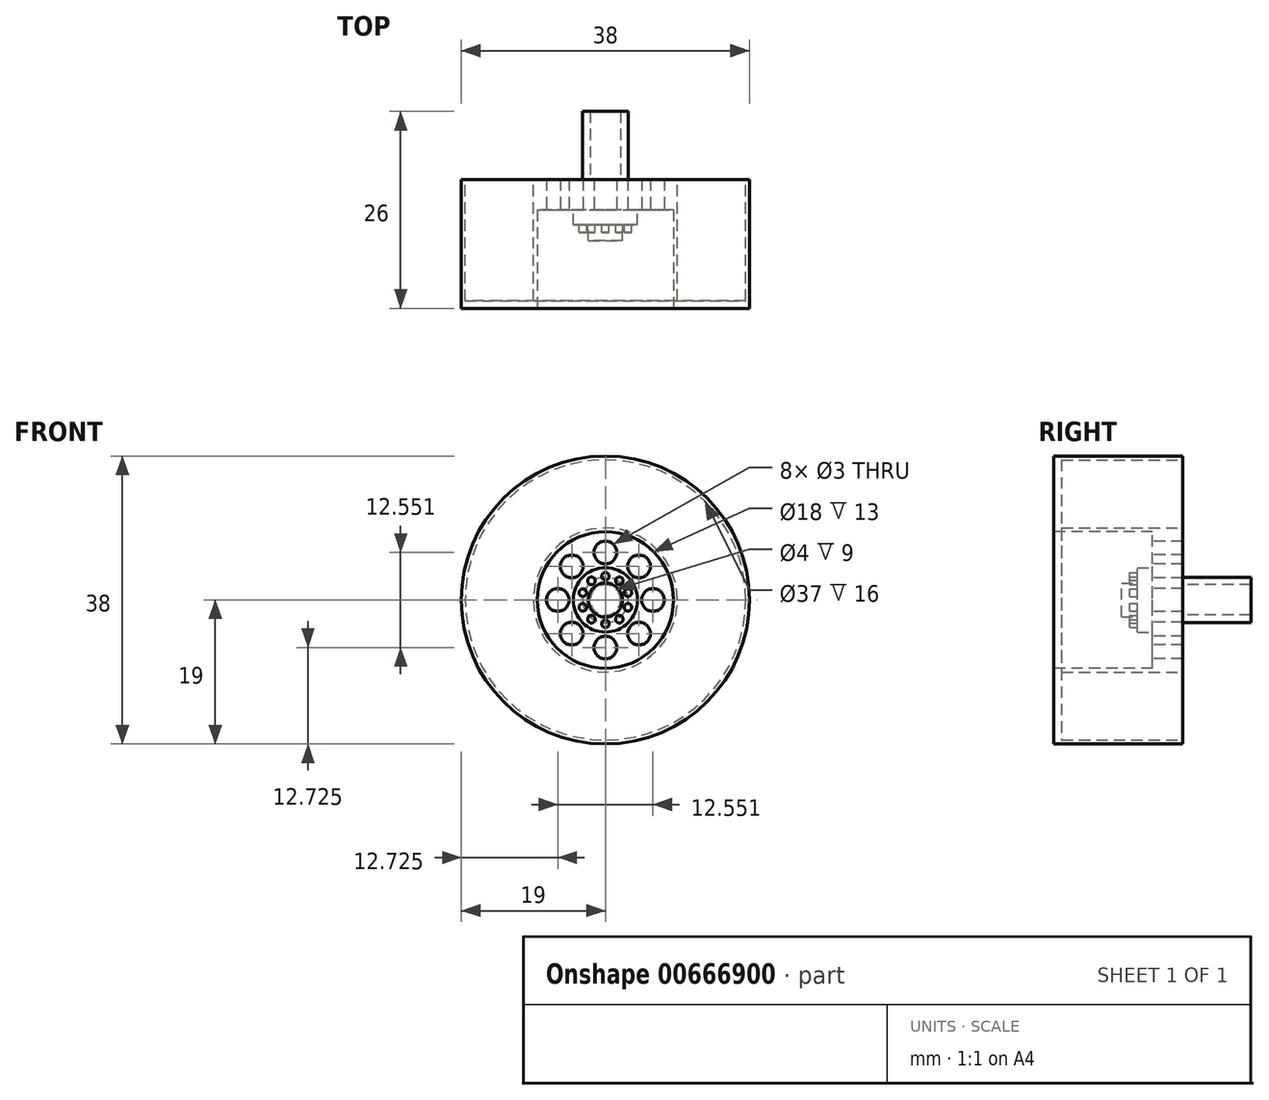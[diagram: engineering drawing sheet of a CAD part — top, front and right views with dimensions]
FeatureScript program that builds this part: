
annotation { "Feature Type Name" : "Feature", "Feature Type Description" : "" }
export const myFeature = defineFeature(function(context is Context, id is Id, definition is map)
    precondition{}
    {
        {
            var Q0;
            Q0=qCreatedBy(makeId("Front.planeOp"),FACE);
            var sketch = newSketch(context, id + "F0", { "sketchPlane" : qUnion([Q0])});
            skCircle(sketch, "E0", {"center": v(0, 0) * mm, "radius": 19 * mm});
            skSolve(sketch);
        }
        {
            var Q0;
            Q0=makeQuery(id+"F0.imprint","IMPRINT",FACE,{"disambiguationData":[TD([[makeQuery(id+"F0.imprint","IMPRINT",EDGE,{"derivedFrom":sQuery(id+"F0.wireOp",EDGE,"E0")}),1.0]])]});
            extrude(context, id + "F1", {"entities" : qUnion([Q0]), "oppositeDirection" : true, "depth" : 17 * mm, "offsetDistance" : 25.4 * mm});
        }
        {
            var Q0;
            Q0=makeQuery(id+"F1.opExtrude","CAP_FACE",FACE,{"disambiguationData":[OSD([sQuery(id+"F0.wireOp",EDGE,"E0")])],"isStart":true});
            var sketch = newSketch(context, id + "F2", { "sketchPlane" : qUnion([Q0])});
            skCircle(sketch, "E1", {"center": v(0, 0) * mm, "radius": 9 * mm});
            skSolve(sketch);
        }
        {
            var Q0;
            Q0=makeQuery(id+"F2.imprint","IMPRINT",FACE,{"disambiguationData":[TD([[makeQuery(id+"F2.imprint","IMPRINT",EDGE,{"derivedFrom":sQuery(id+"F2.wireOp",EDGE,"E1")}),1.0]])]});
            extrude(context, id + "F3", {"entities" : qUnion([Q0]), "operationType" : NewBodyOperationType.REMOVE, "oppositeDirection" : true, "depth" : 13 * mm, "offsetDistance" : 25.4 * mm});
        }
        {
            var Q0;
            Q0=makeQuery(id+"F3.boolean.opBoolean","COPY",FACE,{"derivedFrom":makeQuery(id+"F3.opExtrude","CAP_FACE",FACE,{"disambiguationData":[OSD([sQuery(id+"F2.wireOp",EDGE,"E1")])],"isStart":false})});
            var sketch = newSketch(context, id + "F4", { "sketchPlane" : qUnion([Q0])});
            skCircle(sketch, "E2", {"center": v(0, 6.28) * mm, "radius": 1.5 * mm});
            skCircle(sketch, "E3.1.0", {"center": v(-4.44, 4.44) * mm, "radius": 1.5 * mm});
            skCircle(sketch, "E3.2.0", {"center": v(-6.28, 0) * mm, "radius": 1.5 * mm});
            skCircle(sketch, "E3.3.0", {"center": v(-4.44, -4.44) * mm, "radius": 1.5 * mm});
            skCircle(sketch, "E3.4.0", {"center": v(0, -6.28) * mm, "radius": 1.5 * mm});
            skCircle(sketch, "E3.5.0", {"center": v(4.44, -4.44) * mm, "radius": 1.5 * mm});
            skCircle(sketch, "E3.6.0", {"center": v(6.28, 0) * mm, "radius": 1.5 * mm});
            skCircle(sketch, "E3.7.0", {"center": v(4.44, 4.44) * mm, "radius": 1.5 * mm});
            skPoint(sketch, "E3.center", {"position": v(0, 0) * mm});
            skSolve(sketch);
        }
        {
            var Q0;
            Q0=makeQuery(id+"F4.imprint","IMPRINT",FACE,{"disambiguationData":[TD([[makeQuery(id+"F4.imprint","IMPRINT",EDGE,{"derivedFrom":sQuery(id+"F4.wireOp",EDGE,"E2")}),1.0]])]});
            var Q1;
            Q1=makeQuery(id+"F4.imprint","IMPRINT",FACE,{"disambiguationData":[TD([[makeQuery(id+"F4.imprint","IMPRINT",EDGE,{"derivedFrom":sQuery(id+"F4.wireOp",EDGE,"E3.7.0")}),1.0]])]});
            var Q2;
            Q2=makeQuery(id+"F4.imprint","IMPRINT",FACE,{"disambiguationData":[TD([[makeQuery(id+"F4.imprint","IMPRINT",EDGE,{"derivedFrom":sQuery(id+"F4.wireOp",EDGE,"E3.6.0")}),1.0]])]});
            var Q3;
            Q3=makeQuery(id+"F4.imprint","IMPRINT",FACE,{"disambiguationData":[TD([[makeQuery(id+"F4.imprint","IMPRINT",EDGE,{"derivedFrom":sQuery(id+"F4.wireOp",EDGE,"E3.5.0")}),1.0]])]});
            var Q4;
            Q4=makeQuery(id+"F4.imprint","IMPRINT",FACE,{"disambiguationData":[TD([[makeQuery(id+"F4.imprint","IMPRINT",EDGE,{"derivedFrom":sQuery(id+"F4.wireOp",EDGE,"E3.4.0")}),1.0]])]});
            var Q5;
            Q5=makeQuery(id+"F4.imprint","IMPRINT",FACE,{"disambiguationData":[TD([[makeQuery(id+"F4.imprint","IMPRINT",EDGE,{"derivedFrom":sQuery(id+"F4.wireOp",EDGE,"E3.3.0")}),1.0]])]});
            var Q6;
            Q6=makeQuery(id+"F4.imprint","IMPRINT",FACE,{"disambiguationData":[TD([[makeQuery(id+"F4.imprint","IMPRINT",EDGE,{"derivedFrom":sQuery(id+"F4.wireOp",EDGE,"E3.2.0")}),1.0]])]});
            var Q7;
            Q7=makeQuery(id+"F4.imprint","IMPRINT",FACE,{"disambiguationData":[TD([[makeQuery(id+"F4.imprint","IMPRINT",EDGE,{"derivedFrom":sQuery(id+"F4.wireOp",EDGE,"E3.1.0")}),1.0]])]});
            extrude(context, id + "F5", {"entities" : qUnion([Q0, Q1, Q2, Q3, Q4, Q5, Q6, Q7]), "operationType" : NewBodyOperationType.REMOVE, "oppositeDirection" : true, "depth" : 25 * mm, "offsetDistance" : 25 * mm});
        }
        {
            var Q0;
            Q0=makeQuery(id+"F3.boolean.opBoolean","COPY",FACE,{"derivedFrom":makeQuery(id+"F3.opExtrude","CAP_FACE",FACE,{"disambiguationData":[OSD([sQuery(id+"F2.wireOp",EDGE,"E1")])],"isStart":false})});
            var sketch = newSketch(context, id + "F6", { "sketchPlane" : qUnion([Q0])});
            skCircle(sketch, "E4", {"center": v(0, 0) * mm, "radius": 4.25 * mm});
            skSolve(sketch);
        }
        {
            var Q0;
            Q0=makeQuery(id+"F6.imprint","IMPRINT",FACE,{"disambiguationData":[TD([[makeQuery(id+"F6.imprint","IMPRINT",EDGE,{"derivedFrom":sQuery(id+"F6.wireOp",EDGE,"E4")}),1.0]])]});
            extrude(context, id + "F7", {"entities" : qUnion([Q0]), "operationType" : NewBodyOperationType.ADD, "depth" : 2 * mm, "offsetDistance" : 25 * mm});
        }
        {
            var Q0;
            Q0=makeQuery(id+"F7.opExtrude","CAP_FACE",FACE,{"disambiguationData":[OSD([sQuery(id+"F6.wireOp",EDGE,"E4")])],"isStart":false});
            var sketch = newSketch(context, id + "F8", { "sketchPlane" : qUnion([Q0])});
            skCircle(sketch, "E5", {"center": v(0, 0) * mm, "radius": 2.25 * mm});
            skSolve(sketch);
        }
        {
            var Q0;
            Q0=makeQuery(id+"F8.imprint","IMPRINT",FACE,{"disambiguationData":[TD([[makeQuery(id+"F8.imprint","IMPRINT",EDGE,{"derivedFrom":sQuery(id+"F8.wireOp",EDGE,"E5")}),1.0]])]});
            extrude(context, id + "F9", {"entities" : qUnion([Q0]), "operationType" : NewBodyOperationType.ADD, "depth" : 2.1 * mm, "offsetDistance" : 25 * mm});
        }
        {
            var Q0;
            Q0=makeQuery(id+"F7.opExtrude","CAP_FACE",FACE,{"disambiguationData":[OSD([sQuery(id+"F6.wireOp",EDGE,"E4")])],"isStart":false});
            var sketch = newSketch(context, id + "F10", { "sketchPlane" : qUnion([Q0])});
            skCircle(sketch, "E6", {"center": v(0, 3.13) * mm, "radius": 0.5 * mm});
            skCircle(sketch, "E7.1.0", {"center": v(-1.84, 2.53) * mm, "radius": 0.5 * mm});
            skCircle(sketch, "E7.2.0", {"center": v(-2.98, 0.97) * mm, "radius": 0.5 * mm});
            skCircle(sketch, "E7.3.0", {"center": v(-2.98, -0.97) * mm, "radius": 0.5 * mm});
            skCircle(sketch, "E7.4.0", {"center": v(-1.84, -2.53) * mm, "radius": 0.5 * mm});
            skCircle(sketch, "E7.5.0", {"center": v(0, -3.13) * mm, "radius": 0.5 * mm});
            skCircle(sketch, "E7.6.0", {"center": v(1.84, -2.53) * mm, "radius": 0.5 * mm});
            skCircle(sketch, "E7.7.0", {"center": v(2.98, -0.97) * mm, "radius": 0.5 * mm});
            skCircle(sketch, "E7.8.0", {"center": v(2.98, 0.97) * mm, "radius": 0.5 * mm});
            skCircle(sketch, "E7.9.0", {"center": v(1.84, 2.53) * mm, "radius": 0.5 * mm});
            skPoint(sketch, "E7.center", {"position": v(0, 0) * mm});
            skSolve(sketch);
        }
        {
            var Q0;
            Q0=makeQuery(id+"F10.imprint","IMPRINT",FACE,{"disambiguationData":[TD([[makeQuery(id+"F10.imprint","IMPRINT",EDGE,{"derivedFrom":sQuery(id+"F10.wireOp",EDGE,"E6")}),1.0]])]});
            var Q1;
            Q1=makeQuery(id+"F10.imprint","IMPRINT",FACE,{"disambiguationData":[TD([[makeQuery(id+"F10.imprint","IMPRINT",EDGE,{"derivedFrom":sQuery(id+"F10.wireOp",EDGE,"E7.9.0")}),1.0]])]});
            var Q2;
            Q2=makeQuery(id+"F10.imprint","IMPRINT",FACE,{"disambiguationData":[TD([[makeQuery(id+"F10.imprint","IMPRINT",EDGE,{"derivedFrom":sQuery(id+"F10.wireOp",EDGE,"E7.8.0")}),1.0]])]});
            var Q3;
            Q3=makeQuery(id+"F10.imprint","IMPRINT",FACE,{"disambiguationData":[TD([[makeQuery(id+"F10.imprint","IMPRINT",EDGE,{"derivedFrom":sQuery(id+"F10.wireOp",EDGE,"E7.7.0")}),1.0]])]});
            var Q4;
            Q4=makeQuery(id+"F10.imprint","IMPRINT",FACE,{"disambiguationData":[TD([[makeQuery(id+"F10.imprint","IMPRINT",EDGE,{"derivedFrom":sQuery(id+"F10.wireOp",EDGE,"E7.6.0")}),1.0]])]});
            var Q5;
            Q5=makeQuery(id+"F10.imprint","IMPRINT",FACE,{"disambiguationData":[TD([[makeQuery(id+"F10.imprint","IMPRINT",EDGE,{"derivedFrom":sQuery(id+"F10.wireOp",EDGE,"E7.5.0")}),1.0]])]});
            var Q6;
            Q6=makeQuery(id+"F10.imprint","IMPRINT",FACE,{"disambiguationData":[TD([[makeQuery(id+"F10.imprint","IMPRINT",EDGE,{"derivedFrom":sQuery(id+"F10.wireOp",EDGE,"E7.4.0")}),1.0]])]});
            var Q7;
            Q7=makeQuery(id+"F10.imprint","IMPRINT",FACE,{"disambiguationData":[TD([[makeQuery(id+"F10.imprint","IMPRINT",EDGE,{"derivedFrom":sQuery(id+"F10.wireOp",EDGE,"E7.3.0")}),1.0]])]});
            var Q8;
            Q8=makeQuery(id+"F10.imprint","IMPRINT",FACE,{"disambiguationData":[TD([[makeQuery(id+"F10.imprint","IMPRINT",EDGE,{"derivedFrom":sQuery(id+"F10.wireOp",EDGE,"E7.2.0")}),1.0]])]});
            var Q9;
            Q9=makeQuery(id+"F10.imprint","IMPRINT",FACE,{"disambiguationData":[TD([[makeQuery(id+"F10.imprint","IMPRINT",EDGE,{"derivedFrom":sQuery(id+"F10.wireOp",EDGE,"E7.1.0")}),1.0]])]});
            extrude(context, id + "F11", {"entities" : qUnion([Q0, Q1, Q2, Q3, Q4, Q5, Q6, Q7, Q8, Q9]), "operationType" : NewBodyOperationType.ADD, "depth" : 1 * mm, "offsetDistance" : 25 * mm});
        }
        {
            var Q0;
            Q0=makeQuery(id+"F1.opExtrude","CAP_FACE",FACE,{"disambiguationData":[OSD([sQuery(id+"F0.wireOp",EDGE,"E0")])],"isStart":false});
            var sketch = newSketch(context, id + "F12", { "sketchPlane" : qUnion([Q0])});
            skCircle(sketch, "E8", {"center": v(0, 0) * mm, "radius": 3 * mm});
            skCircle(sketch, "E9", {"center": v(0, 0) * mm, "radius": 2 * mm});
            skSolve(sketch);
        }
        {
            var Q0;
            Q0=makeQuery(id+"F12.imprint","IMPRINT",FACE,{"disambiguationData":[TD([[makeQuery(id+"F12.imprint","IMPRINT",EDGE,{"derivedFrom":sQuery(id+"F12.wireOp",EDGE,"E8")}),1.0]])]});
            extrude(context, id + "F13", {"entities" : qUnion([Q0]), "operationType" : NewBodyOperationType.ADD, "depth" : 9 * mm, "offsetDistance" : 25 * mm});
        }
        {
            var Q0;
            {var subQ0=sQuery(id+"F0.wireOp",EDGE,"E0");Q0=makeQuery(id+"F13.boolean.opBoolean","SPLIT",FACE,{"disambiguationData":[TD([makeQuery(id+"F1.opExtrude","SWEPT_FACE",FACE,{"disambiguationData":[OSD([subQ0])]})])],"derivedFrom":makeQuery(id+"F1.opExtrude","CAP_FACE",FACE,{"disambiguationData":[OSD([subQ0])],"isStart":false})});}
            var sketch = newSketch(context, id + "F14", { "sketchPlane" : qUnion([Q0])});
            skCircle(sketch, "E10", {"center": v(0, 0) * mm, "radius": 9.5 * mm});
            skSolve(sketch);
        }
        {
            var Q0;
            Q0=makeQuery(id+"F14.imprint","IMPRINT",FACE,{"disambiguationData":[TD([[makeQuery(id+"F14.imprint","IMPRINT",EDGE,{"derivedFrom":sQuery(id+"F14.wireOp",EDGE,"E10")}),-1.0]])]});
            var sketch = newSketch(context, id + "F15", { "sketchPlane" : qUnion([Q0])});
            skCircle(sketch, "E11", {"center": v(0, 0) * mm, "radius": 18.5 * mm});
            skSolve(sketch);
        }
        {
            var Q0;
            Q0=makeQuery(id+"F15.imprint","IMPRINT",FACE,{"disambiguationData":[TD([[makeQuery(id+"F15.imprint","IMPRINT",EDGE,{"derivedFrom":sQuery(id+"F15.wireOp",EDGE,"E11")}),1.0]])]});
            extrude(context, id + "F16", {"entities" : qUnion([Q0]), "operationType" : NewBodyOperationType.REMOVE, "oppositeDirection" : true, "depth" : 16 * mm, "offsetDistance" : 25 * mm});
        }
    });
